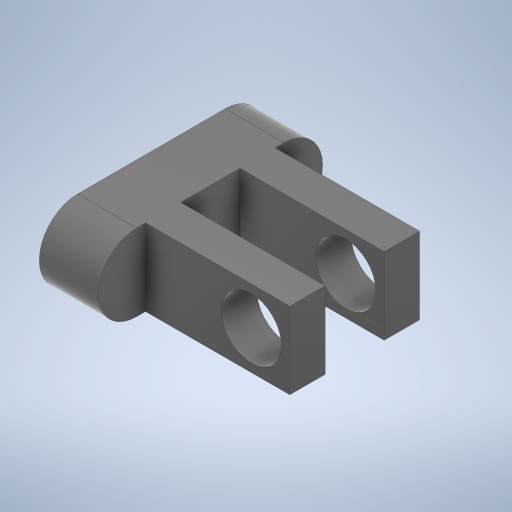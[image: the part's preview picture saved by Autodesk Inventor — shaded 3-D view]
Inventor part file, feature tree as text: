
AUTODESK INVENTOR PART (.ipt)
format: ipt  version: 2023 (Build 270158000, 158)  size: 299,520 bytes
history: native  units: mm
features: extrude x5, plane x4, sketch x4
ambient origin geometry x8: Origin, YZ Plane, XZ Plane, XY Plane, X Axis, Y Axis, Z Axis, Center Point
bodies: Volumenkörper1 (feature_tree)
feature tree (13):
  extrude  "Extrusion1"  Depth=13.0mm
  extrude  "Extrusion2"  Depth=12.5mm
  plane  "Arbeitsebene1"
  extrude  "Extrusion3"  Depth=10.0mm
  plane  "Arbeitsebene2"
  extrude  "Extrusion4"  Depth=6.0mm TaperAngle=0.0deg
  extrude  "Extrusion5"  Depth=13.0mm
  plane  "Arbeitsebene3"
  plane  "Arbeitsebene4"
  sketch  "Skizze1"  dims[d0=13.0mm d1=13.0mm]
  sketch  "Skizze2"  dims[d2=12.5mm d3=12.5mm]
  sketch  "Skizze4"  dims[d6=10.0mm d7=0.0mm d8=10.1mm]
  sketch  "Skizze6"  dims[d9=10.1mm d10=6.0mm d11=0.0mm d12=5.0mm d13=6.0mm d14=0.0mm d15=-5.0mm d17=6.0mm d18=0.0mm d20=10.2mm d21=0.0mm d22=0.0mm d24=0.0mm d25=0.0mm d26=24.445639mm d27=13.0mm]
